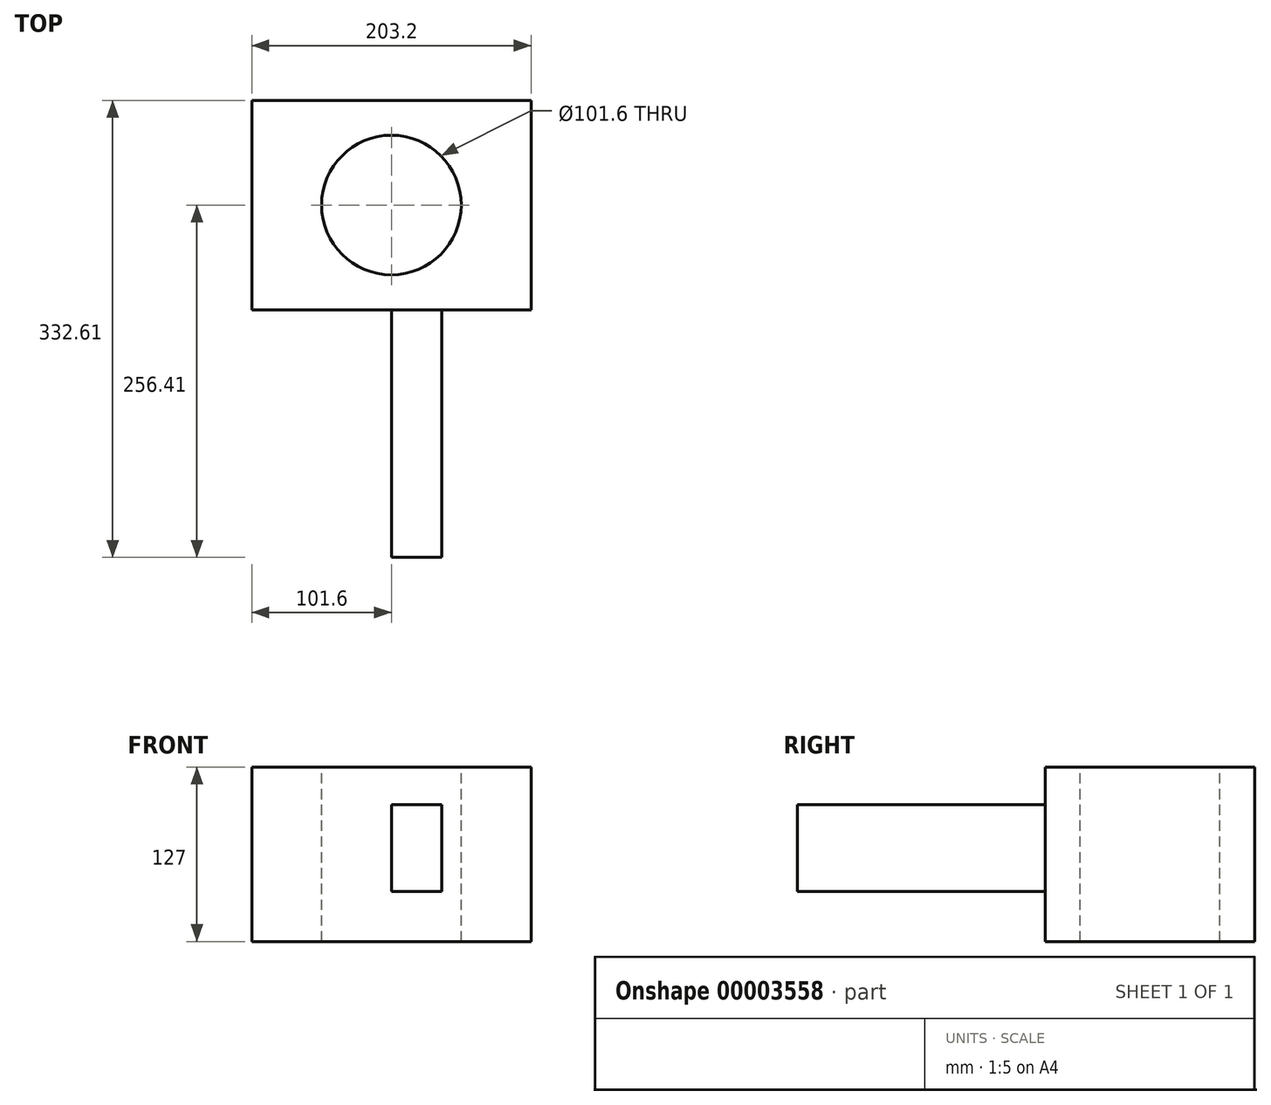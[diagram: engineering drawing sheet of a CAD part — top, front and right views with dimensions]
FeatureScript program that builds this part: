
annotation { "Feature Type Name" : "Feature", "Feature Type Description" : "" }
export const myFeature = defineFeature(function(context is Context, id is Id, definition is map)
    precondition{}
    {
        {
            var Q0;
            Q0=qCreatedBy(makeId("Top.planeOp"),FACE);
            var sketch = newSketch(context, id + "F0", { "sketchPlane" : qUnion([Q0])});
            skLineSegment(sketch, "E0.bottom", {"start": v(-101.6, -76.2) * mm, "end": v(101.6, -76.2) * mm});
            skLineSegment(sketch, "E0.top", {"start": v(-101.6, 76.2) * mm, "end": v(101.6, 76.2) * mm});
            skLineSegment(sketch, "E0.left", {"start": v(-101.6, -76.2) * mm, "end": v(-101.6, 76.2) * mm});
            skLineSegment(sketch, "E0.right", {"start": v(101.6, -76.2) * mm, "end": v(101.6, 76.2) * mm});
            skLineSegment(sketch, "E1", {"start": v(-101.6, 76.2) * mm, "end": v(101.6, -76.2) * mm, "construction": true});
            skSolve(sketch);
        }
        {
            var Q0;
            Q0=makeQuery(id+"F0.imprint","IMPRINT",FACE,{"disambiguationData":[TD([[makeQuery(id+"F0.imprint","IMPRINT",EDGE,{"derivedFrom":sQuery(id+"F0.wireOp",EDGE,"E0.bottom")}),1.0]])]});
            extrude(context, id + "F1", {"entities" : qUnion([Q0]), "endBound" : BoundingType.SYMMETRIC, "depth" : 127 * mm});
        }
        {
            var Q0;
            Q0=makeQuery(id+"F1.opExtrude","CAP_FACE",FACE,{"disambiguationData":[OSD([sQuery(id+"F0.wireOp",EDGE,"E0.bottom"),sQuery(id+"F0.wireOp",EDGE,"E0.top"),sQuery(id+"F0.wireOp",EDGE,"E0.left"),sQuery(id+"F0.wireOp",EDGE,"E0.right")])],"isStart":false});
            var sketch = newSketch(context, id + "F2", { "sketchPlane" : qUnion([Q0])});
            skCircle(sketch, "E2", {"center": v(0, 0) * mm, "radius": 50.8 * mm});
            skLineSegment(sketch, "E3", {"start": v(-101.6, 76.2) * mm, "end": v(101.6, -76.2) * mm, "construction": true});
            skSolve(sketch);
        }
        {
            var Q0;
            Q0=makeQuery(id+"F2.imprint","IMPRINT",FACE,{"disambiguationData":[TD([[makeQuery(id+"F2.imprint","IMPRINT",EDGE,{"derivedFrom":sQuery(id+"F2.wireOp",EDGE,"E2")}),1.0]])]});
            extrude(context, id + "F3", {"entities" : qUnion([Q0]), "operationType" : NewBodyOperationType.REMOVE, "endBound" : BoundingType.UP_TO_NEXT, "oppositeDirection" : true, "depth" : 25.4 * mm});
        }
        {
            var Q0;
            Q0=makeQuery(id+"F1.opExtrude","SWEPT_FACE",FACE,{"disambiguationData":[OSD([sQuery(id+"F0.wireOp",EDGE,"E0.bottom")])]});
            var sketch = newSketch(context, id + "F4", { "sketchPlane" : qUnion([Q0])});
            skLineSegment(sketch, "E4.bottom", {"start": v(0, 36.03) * mm, "end": v(36.52, 36.03) * mm});
            skLineSegment(sketch, "E4.top", {"start": v(0, -27.24) * mm, "end": v(36.52, -27.24) * mm});
            skLineSegment(sketch, "E4.left", {"start": v(0, 36.03) * mm, "end": v(0, -27.24) * mm});
            skLineSegment(sketch, "E4.right", {"start": v(36.52, 36.03) * mm, "end": v(36.52, -27.24) * mm});
            skSolve(sketch);
        }
        {
            var Q0;
            Q0=makeQuery(id+"F4.imprint","IMPRINT",FACE,{"disambiguationData":[TD([[makeQuery(id+"F4.imprint","IMPRINT",EDGE,{"derivedFrom":sQuery(id+"F4.wireOp",EDGE,"E4.bottom")}),-1.0]])]});
            extrude(context, id + "F5", {"entities" : qUnion([Q0]), "operationType" : NewBodyOperationType.ADD, "depth" : 180.2 * mm});
        }
    });
